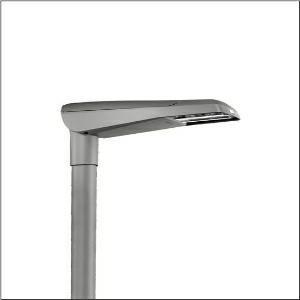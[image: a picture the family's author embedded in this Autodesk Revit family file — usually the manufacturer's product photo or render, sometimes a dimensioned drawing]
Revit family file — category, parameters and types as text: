
# Revit family: streetlight_sl_11_iq_micro___st0_5a_5xc1b41f08ce_e569
name_source: partatom
category: Lighting Fixtures
units: mm (PartAtom-declared; Revit-internal decimal feet)

## family parameters
Cut with Voids When Loaded = No
Host = Face
Light Source = No
Part Type = Normal
Room Calculation Point = No
Round Connector Dimension = Use Diameter
Shared = No

## types (1)
- --- (1 x LED, 1940 lm, 12.6 W, 4000K)
    Apparent Load = 13 VA
    CIE Flux Codes = 42 72 97 100 100
    Color Rendering = 70
    Color Temperature = 4000K
    Default Elevation = 1800 mm
    Description = Streetlight SL 11 iQ micro, mast luminaire, primary light control with 3 zone facetted reflector, of plastic, silver coated, highly specular, primary optical cover: cover, of PMMA, transparent, light distribution: ST0.5a, light emission: direct distribution, primary light characteristic: asymmetric, installation type: post-top, side-entry, lamps: LED, High Power LED, rated values: 1.940lm | 12,6W | 154lm/W (begin service life); end service life: 1.940lm | 12,9W; at 50% lumin. flux: 970lm | 6,8W | 142,6lm/W, colour temperature: 4000K, colour rendering: CRI > 70, light colour: 740, light setting 1 begin service life: 100% | 1.940lm | 12,6W | 154lm/W | 4.000K, light setting 1 end service life: 12,9W, further light settings possible, control: Street-Remote, optimised constant luminous flux control (CLO 2.0), Desk-Remote (wireless, voltage-free reading and setting of iQ features in the workshop via application-optimized NFC function/RFID function), Light-Fading, Smart-Wire, Night-Set, Lumen-Switch, Temp-Guard, Auto-Match, with cable H07RN-F 5x 1.5mm², mains connection: 230..240V, AC, 50/60Hz, connection cable pre-assembled, cable length: 5,5m, luminaire housing, of diecast aluminium, powder-coated, Siteco® metallic grey (DB 702S), please order mast flange separately, inclination adjustable without tools: 0°, 5°, 10°, 15° (post-top) | 0°, -5°, -10°, -15° (side-entry), sealing non-destructively replaceable, multi-level sealing system, length: 600mm, width: 174mm, height: 116mm, mast flange for spigot size: 42mm (side-entry): 5XC10008XM4, 60/48mm (side-entry/post-top): 5XC10108XM2, 76/60mm (side-entry/post-top): 5XC10108XM1, equipment: standard, protection rating (complete): IP66, insulation class (complete): insulation class II (safety insulation), certification: CE, ENEC, ENEC+, VDE, impact resistance: IK10, permissible operating ambient temperature for outdoor applications: -25..+50°C, standard-compliant lighting for roads and squares, Environmental Product Declaration (EPD) tested and certified by an independent institute, packaging unit: 1 piece

Light Distribution: ST0.5a
    Height = 116 mm
    Lamp = 1 x LED
    Lamp Light Flux = 1940 lm
    Lamp Power = 12.6 W
    Lamp count = 1
    Length = 600 mm
    Luminous efficacy = 154 lm/W
    Manufacturer = Siteco
    ModVariant = No
    Model = 5XC1B41F08CE
    Number of Poles = 1
    OnlyDefault = Yes
    Power Factor = 1
    Product Name = Streetlight SL 11 iQ micro | ST0.5a
    Product group = mast luminaire | pylon top
    ProductGroupID = 6100
    Protection Class = Protection class II
    Protection Degree = IP 66
    RLX_Detail_Level = 1
    RLX_Emergency_Light_Flux = 0 lm
    RLX_Emergency_Type = 0
    RLX_Emergency_Type_DB = No
    RlxData = <blob elided: 26681 chars, md5=e1aa02fa>
    Socket = socket
    Standby Power = 0 W
    System Light Flux = 1940 lm
    System Power = 13 W
    Type Comments = factory setting: luminous flux: 100 % | dim-lin: 254 | 229 mA
    Type Image = l_1006566.jpg
    URL = http://relux.com
    VarID = @adj_020725
    Voltage = 0 V
    Weight = 0.00 kg
    Width = 174 mm

## geometry (parser evidence)
native form markers: Blend x4, Sweep x11
no freeform markers — native parametric forms only
